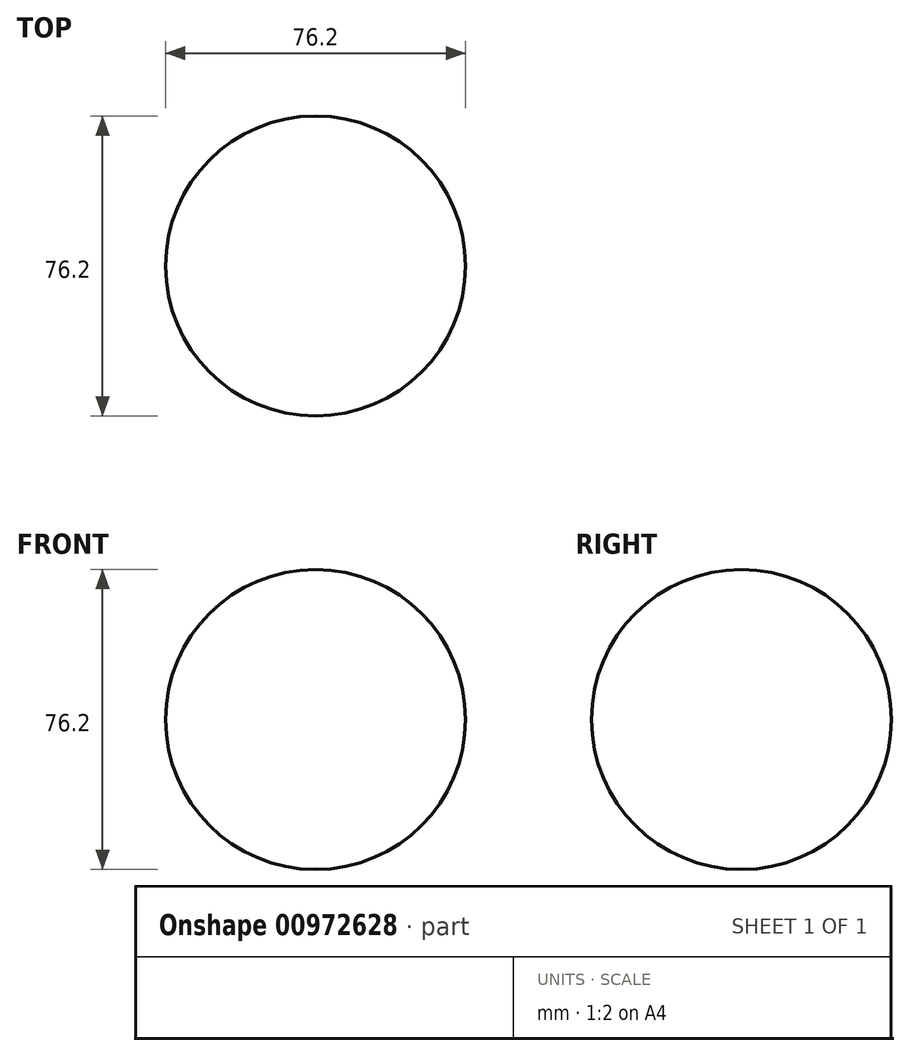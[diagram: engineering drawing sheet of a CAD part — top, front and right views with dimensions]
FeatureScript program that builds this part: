
annotation { "Feature Type Name" : "Feature", "Feature Type Description" : "" }
export const myFeature = defineFeature(function(context is Context, id is Id, definition is map)
    precondition{}
    {
        {
            var Q0;
            Q0=qCreatedBy(makeId("Front.planeOp"),FACE);
            var sketch = newSketch(context, id + "F0", { "sketchPlane" : qUnion([Q0])});
            skArc(sketch, "E0", {"start": v(0, 38.1) * mm, "mid": v(-38.1, 0) * mm, "end": v(0, -38.1) * mm});
            skLineSegment(sketch, "E1", {"start": v(0, 38.1) * mm, "end": v(0, -38.1) * mm});
            skSolve(sketch);
        }
        {
            var Q0;
            Q0 = qSketchRegion(id + "F0", true);
            var Q1;
            Q1=sQuery(id+"F0.wireOp",EDGE,"E1");
            revolve(context, id + "F1", {"surfaceOperationType" : NewSurfaceOperationType.NEW, "entities" : qUnion([Q0]), "axis" : qUnion([Q1]), "revolveType" : RevolveType.ONE_DIRECTION, "angle" : 360 * degree});
        }
    });
